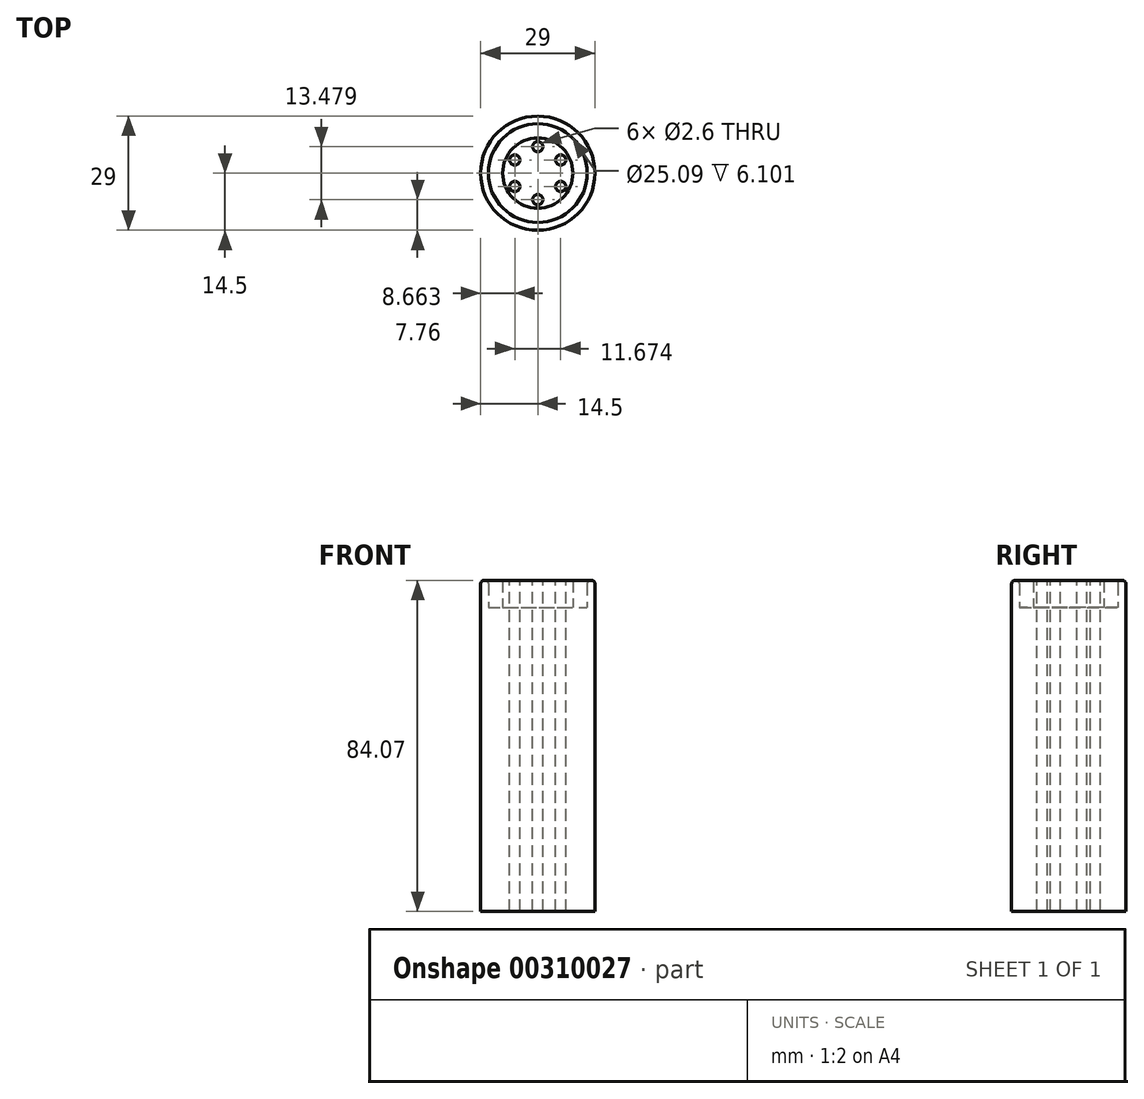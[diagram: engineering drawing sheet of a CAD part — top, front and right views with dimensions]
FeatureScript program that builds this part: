
annotation { "Feature Type Name" : "Feature", "Feature Type Description" : "" }
export const myFeature = defineFeature(function(context is Context, id is Id, definition is map)
    precondition{}
    {
        {
            var Q0;
            Q0=qCreatedBy(makeId("Top.planeOp"),FACE);
            var sketch = newSketch(context, id + "F0", { "sketchPlane" : qUnion([Q0])});
            skCircle(sketch, "E0", {"center": v(0, 0) * mm, "radius": 14.5 * mm});
            skSolve(sketch);
        }
        {
            var Q0;
            Q0 = qSketchRegion(id + "F0", true);
            extrude(context, id + "F1", {"entities" : qUnion([Q0]), "depth" : 84.07 * mm});
        }
        {
            var Q0;
            Q0=makeQuery(id+"F1.opExtrude","CAP_FACE",FACE,{"disambiguationData":[OSD([sQuery(id+"F0.wireOp",EDGE,"E0")])],"isStart":false});
            var sketch = newSketch(context, id + "F2", { "sketchPlane" : qUnion([Q0])});
            skCircle(sketch, "E1", {"center": v(0, 6.74) * mm, "radius": 1.3 * mm});
            skCircle(sketch, "E2.1.0", {"center": v(-5.84, 3.37) * mm, "radius": 1.3 * mm});
            skCircle(sketch, "E2.2.0", {"center": v(-5.84, -3.37) * mm, "radius": 1.3 * mm});
            skCircle(sketch, "E2.3.0", {"center": v(0, -6.74) * mm, "radius": 1.3 * mm});
            skCircle(sketch, "E2.4.0", {"center": v(5.84, -3.37) * mm, "radius": 1.3 * mm});
            skCircle(sketch, "E2.5.0", {"center": v(5.84, 3.37) * mm, "radius": 1.3 * mm});
            skPoint(sketch, "E2.center", {"position": v(0, 0) * mm});
            skSolve(sketch);
        }
        {
            var Q0;
            Q0=makeQuery(id+"F2.imprint","IMPRINT",FACE,{"disambiguationData":[TD([[makeQuery(id+"F2.imprint","IMPRINT",EDGE,{"derivedFrom":sQuery(id+"F2.wireOp",EDGE,"E1")}),1.0]])]});
            var Q1;
            Q1=makeQuery(id+"F2.imprint","IMPRINT",FACE,{"disambiguationData":[TD([[makeQuery(id+"F2.imprint","IMPRINT",EDGE,{"derivedFrom":sQuery(id+"F2.wireOp",EDGE,"E2.5.0")}),1.0]])]});
            var Q2;
            Q2=makeQuery(id+"F2.imprint","IMPRINT",FACE,{"disambiguationData":[TD([[makeQuery(id+"F2.imprint","IMPRINT",EDGE,{"derivedFrom":sQuery(id+"F2.wireOp",EDGE,"E2.4.0")}),1.0]])]});
            var Q3;
            Q3=makeQuery(id+"F2.imprint","IMPRINT",FACE,{"disambiguationData":[TD([[makeQuery(id+"F2.imprint","IMPRINT",EDGE,{"derivedFrom":sQuery(id+"F2.wireOp",EDGE,"E2.3.0")}),1.0]])]});
            var Q4;
            Q4=makeQuery(id+"F2.imprint","IMPRINT",FACE,{"disambiguationData":[TD([[makeQuery(id+"F2.imprint","IMPRINT",EDGE,{"derivedFrom":sQuery(id+"F2.wireOp",EDGE,"E2.2.0")}),1.0]])]});
            var Q5;
            Q5=makeQuery(id+"F2.imprint","IMPRINT",FACE,{"disambiguationData":[TD([[makeQuery(id+"F2.imprint","IMPRINT",EDGE,{"derivedFrom":sQuery(id+"F2.wireOp",EDGE,"E2.1.0")}),1.0]])]});
            extrude(context, id + "F3", {"entities" : qUnion([Q0, Q1, Q2, Q3, Q4, Q5]), "operationType" : NewBodyOperationType.REMOVE, "endBound" : BoundingType.THROUGH_ALL, "oppositeDirection" : true, "depth" : 25.4 * mm});
        }
        {
            var Q0;
            Q0=qCreatedBy(makeId("Front.planeOp"),FACE);
            var sketch = newSketch(context, id + "F4", { "sketchPlane" : qUnion([Q0])});
            skLineSegment(sketch, "E3.bottom", {"start": v(8.92, 77.18) * mm, "end": v(12.55, 77.18) * mm});
            skLineSegment(sketch, "E3.top", {"start": v(8.92, 85.33) * mm, "end": v(12.55, 85.33) * mm});
            skLineSegment(sketch, "E3.left", {"start": v(8.92, 77.18) * mm, "end": v(8.92, 85.33) * mm});
            skLineSegment(sketch, "E3.right", {"start": v(12.55, 77.18) * mm, "end": v(12.55, 85.33) * mm});
            skPoint(sketch, "E3.middle", {"position": v(10.73, 81.25) * mm});
            skSolve(sketch);
        }
        {
            var Q0;
            Q0 = qSketchRegion(id + "F4", true);
            var Q1;
            Q1=makeQuery(id+"F1.opExtrude","SWEPT_FACE",FACE,{"disambiguationData":[OSD([sQuery(id+"F0.wireOp",EDGE,"E0")])]});
            revolve(context, id + "F5", {"operationType" : NewBodyOperationType.REMOVE, "entities" : qUnion([Q0]), "axis" : qUnion([Q1]), "revolveType" : RevolveType.FULL, "oppositeDirection" : true});
        }
        {
            var Q0;
            {var subQ0=sQuery(id+"F0.wireOp",EDGE,"E0");Q0=makeQuery(id+"F5.boolean.opBoolean","SPLIT",FACE,{"disambiguationData":[TD([makeQuery(id+"F1.opExtrude","SWEPT_FACE",FACE,{"disambiguationData":[OSD([subQ0])]})])],"derivedFrom":makeQuery(id+"F1.opExtrude","CAP_FACE",FACE,{"disambiguationData":[OSD([subQ0])],"isStart":false})});}
            fillet(context, id + "F6", {"entities" : qUnion([Q0]), "radius" : 0.8 * mm, "tangentPropagation" : true, "allowEdgeOverflow" : false});
        }
    });
